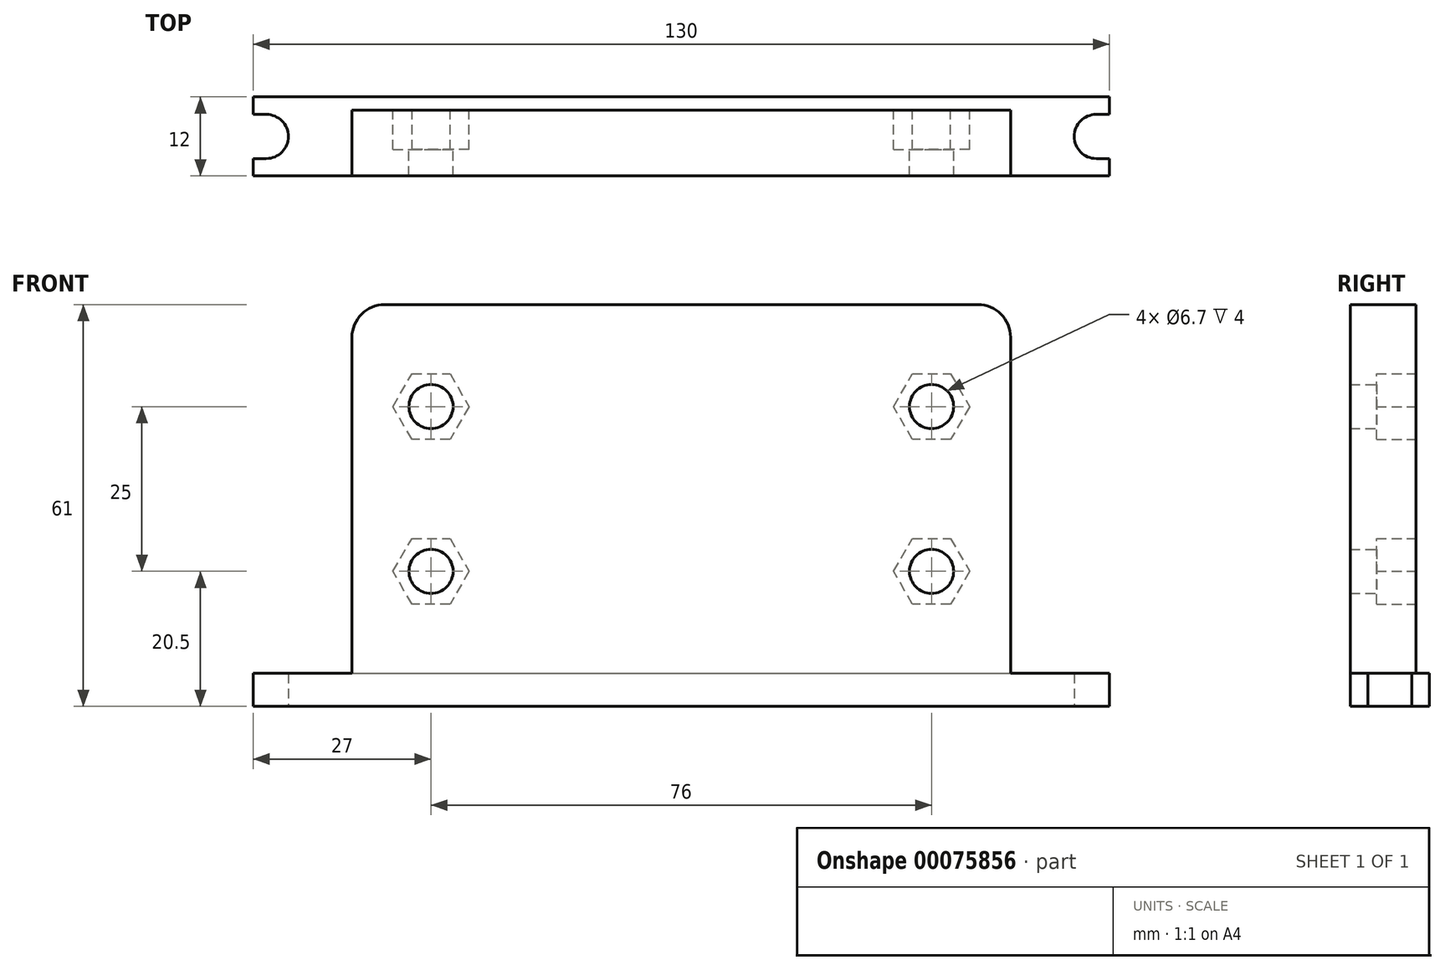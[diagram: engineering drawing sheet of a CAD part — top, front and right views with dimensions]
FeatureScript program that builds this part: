
annotation { "Feature Type Name" : "Feature", "Feature Type Description" : "" }
export const myFeature = defineFeature(function(context is Context, id is Id, definition is map)
    precondition{}
    {
        {
            var Q0;
            Q0=qCreatedBy(makeId("Front.planeOp"),FACE);
            var sketch = newSketch(context, id + "F0", { "sketchPlane" : qUnion([Q0])});
            skLineSegment(sketch, "E0", {"start": v(-65, 0) * mm, "end": v(-65, 5) * mm});
            skLineSegment(sketch, "E1", {"start": v(-65, 5) * mm, "end": v(-50, 5) * mm});
            skLineSegment(sketch, "E2", {"start": v(-50, 5) * mm, "end": v(-50, 61) * mm});
            skLineSegment(sketch, "E3", {"start": v(-50, 61) * mm, "end": v(50, 61) * mm});
            skLineSegment(sketch, "E4", {"start": v(50, 61) * mm, "end": v(50, 5) * mm});
            skLineSegment(sketch, "E5", {"start": v(50, 5) * mm, "end": v(65, 5) * mm});
            skLineSegment(sketch, "E6", {"start": v(65, 5) * mm, "end": v(65, 0) * mm});
            skLineSegment(sketch, "E7", {"start": v(65, 0) * mm, "end": v(-65, 0) * mm});
            skLineSegment(sketch, "E8", {"start": v(-66.2, 33) * mm, "end": v(67.97, 33) * mm, "construction": true});
            skCircle(sketch, "E9", {"center": v(-38, 45.5) * mm, "radius": 3.35 * mm});
            skCircle(sketch, "E10", {"center": v(38, 45.5) * mm, "radius": 3.35 * mm});
            skCircle(sketch, "E11", {"center": v(-38, 20.5) * mm, "radius": 3.35 * mm});
            skCircle(sketch, "E12", {"center": v(38, 20.5) * mm, "radius": 3.35 * mm});
            skLineSegment(sketch, "E13.bottom", {"start": v(-38, 45.5) * mm, "end": v(38, 45.5) * mm, "construction": true});
            skLineSegment(sketch, "E13.top", {"start": v(-38, 20.5) * mm, "end": v(38, 20.5) * mm, "construction": true});
            skLineSegment(sketch, "E13.left", {"start": v(-38, 45.5) * mm, "end": v(-38, 20.5) * mm, "construction": true});
            skLineSegment(sketch, "E13.right", {"start": v(38, 45.5) * mm, "end": v(38, 20.5) * mm, "construction": true});
            skSolve(sketch);
        }
        {
            var Q0;
            Q0 = qSketchRegion(id + "F0", true);
            extrude(context, id + "F1", {"entities" : qUnion([Q0]), "depth" : 12 * mm});
        }
        {
            var Q0;
            Q0=makeQuery(id+"F1.opExtrude","SWEPT_FACE",FACE,{"disambiguationData":[OSD([sQuery(id+"F0.wireOp",EDGE,"E7")])]});
            var sketch = newSketch(context, id + "F2", { "sketchPlane" : qUnion([Q0])});
            skLineSegment(sketch, "E14", {"start": v(-65, 6) * mm, "end": v(65, 6) * mm, "construction": true});
            skArc(sketch, "E15", {"start": v(-63, 2.65) * mm, "mid": v(-59.65, 6) * mm, "end": v(-63, 9.35) * mm});
            skArc(sketch, "E16", {"start": v(63, 9.35) * mm, "mid": v(59.65, 6) * mm, "end": v(63, 2.65) * mm});
            skLineSegment(sketch, "E17", {"start": v(-63, 9.35) * mm, "end": v(-65, 9.35) * mm});
            skLineSegment(sketch, "E18", {"start": v(-63, 2.65) * mm, "end": v(-65, 2.65) * mm});
            skLineSegment(sketch, "E19", {"start": v(-65, 9.35) * mm, "end": v(-65, 2.65) * mm});
            skLineSegment(sketch, "E20", {"start": v(63, 9.35) * mm, "end": v(65, 9.35) * mm});
            skLineSegment(sketch, "E21", {"start": v(63, 2.65) * mm, "end": v(65, 2.65) * mm});
            skLineSegment(sketch, "E22", {"start": v(65, 2.65) * mm, "end": v(65, 9.35) * mm});
            skSolve(sketch);
        }
        {
            var Q0;
            Q0 = qSketchRegion(id + "F2", true);
            extrude(context, id + "F3", {"entities" : qUnion([Q0]), "operationType" : NewBodyOperationType.REMOVE, "endBound" : BoundingType.UP_TO_NEXT, "oppositeDirection" : true, "depth" : 25 * mm});
        }
        {
            var Q0;
            Q0=makeQuery(id+"F1.opExtrude","CAP_FACE",FACE,{"disambiguationData":[OSD([sQuery(id+"F0.wireOp",EDGE,"E0"),sQuery(id+"F0.wireOp",EDGE,"E1"),sQuery(id+"F0.wireOp",EDGE,"E2"),sQuery(id+"F0.wireOp",EDGE,"E3"),sQuery(id+"F0.wireOp",EDGE,"E4"),sQuery(id+"F0.wireOp",EDGE,"E5"),sQuery(id+"F0.wireOp",EDGE,"E6"),sQuery(id+"F0.wireOp",EDGE,"E7"),sQuery(id+"F0.wireOp",EDGE,"E9"),sQuery(id+"F0.wireOp",EDGE,"E10"),sQuery(id+"F0.wireOp",EDGE,"E11"),sQuery(id+"F0.wireOp",EDGE,"E12")])],"isStart":true});
            var sketch = newSketch(context, id + "F4", { "sketchPlane" : qUnion([Q0])});
            skCircle(sketch, "E23.cCircle", {"center": v(38, 20.5) * mm, "radius": 5 * mm, "construction": true});
            skLineSegment(sketch, "E23.0", {"start": v(32.23, 20.5) * mm, "end": v(35.11, 25.5) * mm});
            skLineSegment(sketch, "E23.1", {"start": v(35.11, 25.5) * mm, "end": v(40.89, 25.5) * mm});
            skLineSegment(sketch, "E23.2", {"start": v(40.89, 25.5) * mm, "end": v(43.77, 20.5) * mm});
            skLineSegment(sketch, "E23.3", {"start": v(43.77, 20.5) * mm, "end": v(40.89, 15.5) * mm});
            skLineSegment(sketch, "E23.4", {"start": v(40.89, 15.5) * mm, "end": v(35.11, 15.5) * mm});
            skLineSegment(sketch, "E23.5", {"start": v(35.11, 15.5) * mm, "end": v(32.23, 20.5) * mm});
            skPoint(sketch, "E23.0.midPoint", {"position": v(33.67, 23) * mm});
            skCircle(sketch, "E24.cCircle", {"center": v(-38, 20.5) * mm, "radius": 5 * mm, "construction": true});
            skLineSegment(sketch, "E24.0", {"start": v(-43.77, 20.5) * mm, "end": v(-40.89, 25.5) * mm});
            skLineSegment(sketch, "E24.1", {"start": v(-40.89, 25.5) * mm, "end": v(-35.11, 25.5) * mm});
            skLineSegment(sketch, "E24.2", {"start": v(-35.11, 25.5) * mm, "end": v(-32.23, 20.5) * mm});
            skLineSegment(sketch, "E24.3", {"start": v(-32.23, 20.5) * mm, "end": v(-35.11, 15.5) * mm});
            skLineSegment(sketch, "E24.4", {"start": v(-35.11, 15.5) * mm, "end": v(-40.89, 15.5) * mm});
            skLineSegment(sketch, "E24.5", {"start": v(-40.89, 15.5) * mm, "end": v(-43.77, 20.5) * mm});
            skPoint(sketch, "E24.0.midPoint", {"position": v(-42.33, 23) * mm});
            skCircle(sketch, "E25.cCircle", {"center": v(38, 45.5) * mm, "radius": 5 * mm, "construction": true});
            skLineSegment(sketch, "E25.0", {"start": v(32.23, 45.5) * mm, "end": v(35.11, 50.5) * mm});
            skLineSegment(sketch, "E25.1", {"start": v(35.11, 50.5) * mm, "end": v(40.89, 50.5) * mm});
            skLineSegment(sketch, "E25.2", {"start": v(40.89, 50.5) * mm, "end": v(43.77, 45.5) * mm});
            skLineSegment(sketch, "E25.3", {"start": v(43.77, 45.5) * mm, "end": v(40.89, 40.5) * mm});
            skLineSegment(sketch, "E25.4", {"start": v(40.89, 40.5) * mm, "end": v(35.11, 40.5) * mm});
            skLineSegment(sketch, "E25.5", {"start": v(35.11, 40.5) * mm, "end": v(32.23, 45.5) * mm});
            skPoint(sketch, "E25.0.midPoint", {"position": v(33.67, 48) * mm});
            skCircle(sketch, "E26.cCircle", {"center": v(-38, 45.5) * mm, "radius": 5 * mm, "construction": true});
            skLineSegment(sketch, "E26.0", {"start": v(-43.77, 45.5) * mm, "end": v(-40.89, 50.5) * mm});
            skLineSegment(sketch, "E26.1", {"start": v(-40.89, 50.5) * mm, "end": v(-35.11, 50.5) * mm});
            skLineSegment(sketch, "E26.2", {"start": v(-35.11, 50.5) * mm, "end": v(-32.23, 45.5) * mm});
            skLineSegment(sketch, "E26.3", {"start": v(-32.23, 45.5) * mm, "end": v(-35.11, 40.5) * mm});
            skLineSegment(sketch, "E26.4", {"start": v(-35.11, 40.5) * mm, "end": v(-40.89, 40.5) * mm});
            skLineSegment(sketch, "E26.5", {"start": v(-40.89, 40.5) * mm, "end": v(-43.77, 45.5) * mm});
            skPoint(sketch, "E26.0.midPoint", {"position": v(-42.33, 48) * mm});
            skSolve(sketch);
        }
        {
            var Q0;
            Q0 = qSketchRegion(id + "F4", true);
            extrude(context, id + "F5", {"entities" : qUnion([Q0]), "operationType" : NewBodyOperationType.REMOVE, "oppositeDirection" : true, "depth" : 8 * mm});
        }
        {
            var Q0;
            Q0=makeQuery(id+"F1.opExtrude","CAP_FACE",FACE,{"disambiguationData":[OSD([sQuery(id+"F0.wireOp",EDGE,"E0"),sQuery(id+"F0.wireOp",EDGE,"E1"),sQuery(id+"F0.wireOp",EDGE,"E2"),sQuery(id+"F0.wireOp",EDGE,"E3"),sQuery(id+"F0.wireOp",EDGE,"E4"),sQuery(id+"F0.wireOp",EDGE,"E5"),sQuery(id+"F0.wireOp",EDGE,"E6"),sQuery(id+"F0.wireOp",EDGE,"E7"),sQuery(id+"F0.wireOp",EDGE,"E9"),sQuery(id+"F0.wireOp",EDGE,"E10"),sQuery(id+"F0.wireOp",EDGE,"E11"),sQuery(id+"F0.wireOp",EDGE,"E12")])],"isStart":true});
            var sketch = newSketch(context, id + "F6", { "sketchPlane" : qUnion([Q0])});
            skLineSegment(sketch, "E27.bottom", {"start": v(50, 5) * mm, "end": v(-50, 5) * mm});
            skLineSegment(sketch, "E27.top", {"start": v(50, 61) * mm, "end": v(-50, 61) * mm});
            skLineSegment(sketch, "E27.left", {"start": v(50, 5) * mm, "end": v(50, 61) * mm});
            skLineSegment(sketch, "E27.right", {"start": v(-50, 5) * mm, "end": v(-50, 61) * mm});
            skSolve(sketch);
        }
        {
            var Q0;
            Q0 = qSketchRegion(id + "F6", true);
            extrude(context, id + "F7", {"entities" : qUnion([Q0]), "operationType" : NewBodyOperationType.REMOVE, "oppositeDirection" : true, "depth" : 2 * mm});
        }
        {
            var Q0;
            Q0=makeQuery(id+"F1.opExtrude","SWEPT_EDGE",EDGE,{"disambiguationData":[OSD([sQuery(id+"F0.wireOp",EDGE,"E2"),sQuery(id+"F0.wireOp",EDGE,"E3")])]});
            var Q1;
            Q1=makeQuery(id+"F1.opExtrude","SWEPT_EDGE",EDGE,{"disambiguationData":[OSD([sQuery(id+"F0.wireOp",EDGE,"E3"),sQuery(id+"F0.wireOp",EDGE,"E4")])]});
            fillet(context, id + "F8", {"entities" : qUnion([Q0, Q1]), "radius" : 5 * mm, "tangentPropagation" : true, "allowEdgeOverflow" : false});
        }
    });
